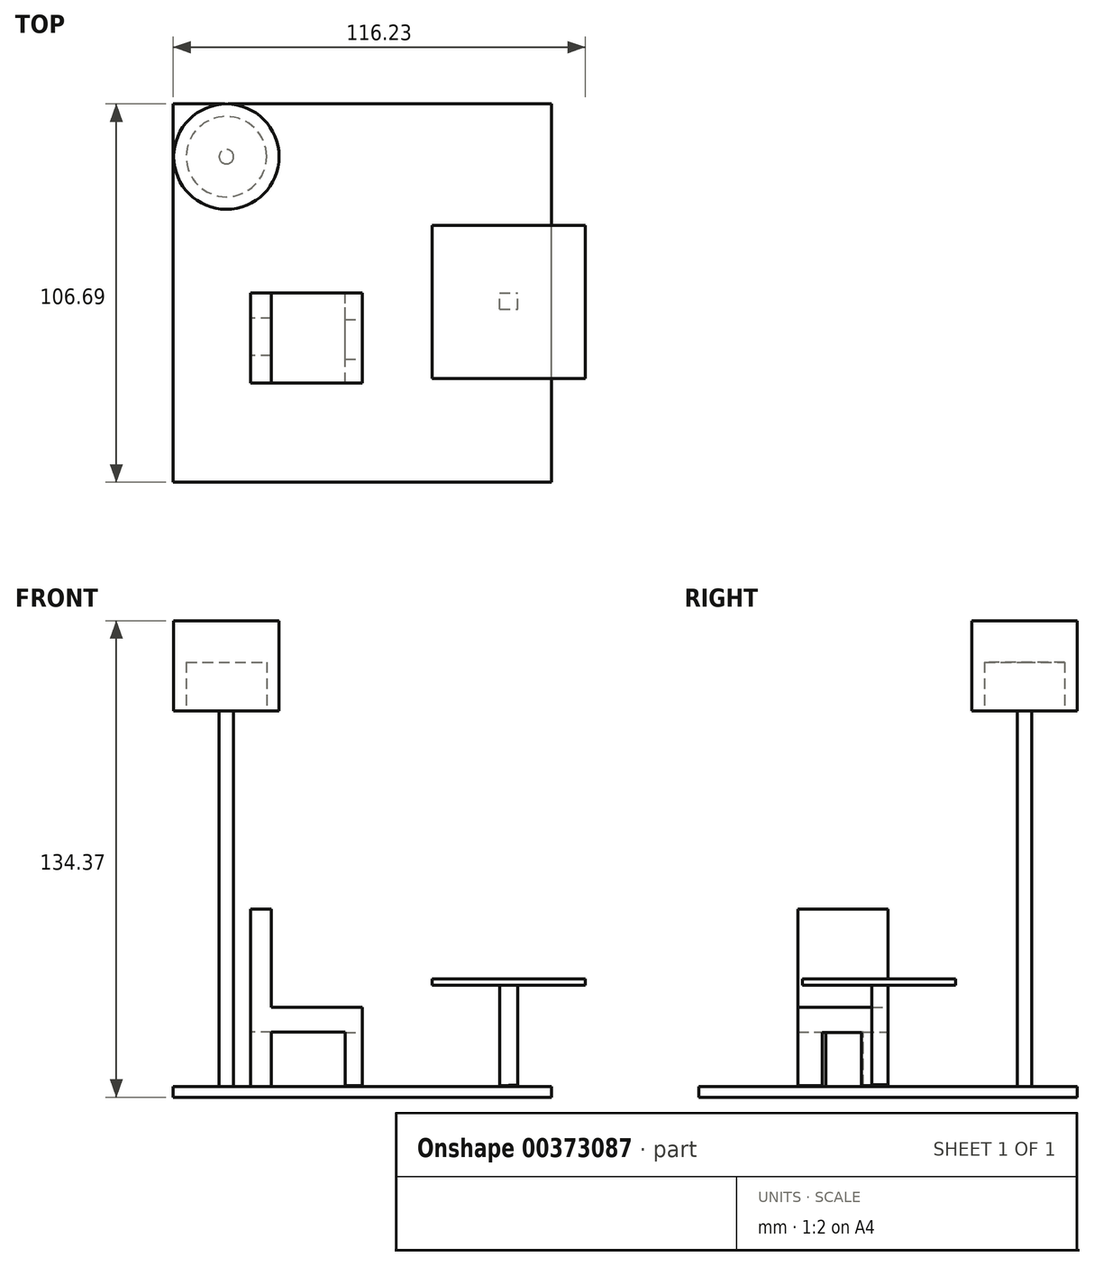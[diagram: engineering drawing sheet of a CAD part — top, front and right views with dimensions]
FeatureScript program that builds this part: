
annotation { "Feature Type Name" : "Feature", "Feature Type Description" : "" }
export const myFeature = defineFeature(function(context is Context, id is Id, definition is map)
    precondition{}
    {
        {
            var Q0;
            Q0=qCreatedBy(makeId("Top.planeOp"),FACE);
            var sketch = newSketch(context, id + "F0", { "sketchPlane" : qUnion([Q0])});
            skLineSegment(sketch, "E0.bottom", {"start": v(53.34, -53.34) * mm, "end": v(-53.34, -53.34) * mm});
            skLineSegment(sketch, "E0.top", {"start": v(53.34, 53.34) * mm, "end": v(-53.34, 53.34) * mm});
            skLineSegment(sketch, "E0.left", {"start": v(53.34, -53.34) * mm, "end": v(53.34, 53.34) * mm});
            skLineSegment(sketch, "E0.right", {"start": v(-53.34, -53.34) * mm, "end": v(-53.34, 53.34) * mm});
            skPoint(sketch, "E0.middle", {"position": v(0, 0) * mm});
            skSolve(sketch);
        }
        {
            var Q0;
            Q0 = qSketchRegion(id + "F0", true);
            extrude(context, id + "F1", {"entities" : qUnion([Q0]), "depth" : 3.05 * mm});
        }
        {
            var Q0;
            Q0=qCreatedBy(makeId("Front.planeOp"),FACE);
            var sketch = newSketch(context, id + "F2", { "sketchPlane" : qUnion([Q0])});
            skLineSegment(sketch, "E1", {"start": v(38.7, 3.2) * mm, "end": v(38.7, 31.55) * mm});
            skLineSegment(sketch, "E2", {"start": v(43.9, 3.5) * mm, "end": v(43.9, 31.55) * mm});
            skLineSegment(sketch, "E3", {"start": v(38.7, 31.55) * mm, "end": v(43.9, 31.55) * mm});
            skLineSegment(sketch, "E4", {"start": v(38.7, 3.2) * mm, "end": v(43.9, 3.5) * mm});
            skSolve(sketch);
        }
        {
            var Q0;
            Q0 = qSketchRegion(id + "F2", true);
            extrude(context, id + "F3", {"entities" : qUnion([Q0]), "depth" : 4.57 * mm});
        }
        {
            var Q0;
            Q0=makeQuery(id+"F3.opExtrude","SWEPT_FACE",FACE,{"disambiguationData":[OSD([sQuery(id+"F2.wireOp",EDGE,"E3")])]});
            var sketch = newSketch(context, id + "F4", { "sketchPlane" : qUnion([Q0])});
            skLineSegment(sketch, "E5.bottom", {"start": v(19.71, -24.09) * mm, "end": v(62.9, -24.09) * mm});
            skLineSegment(sketch, "E5.top", {"start": v(19.71, 19.1) * mm, "end": v(62.9, 19.1) * mm});
            skLineSegment(sketch, "E5.left", {"start": v(19.71, -24.09) * mm, "end": v(19.71, 19.1) * mm});
            skLineSegment(sketch, "E5.right", {"start": v(62.9, -24.09) * mm, "end": v(62.9, 19.1) * mm});
            skPoint(sketch, "E5.middle", {"position": v(41.3, -2.5) * mm});
            skPoint(sketch, "E5.middle.positionSnap0", {"position": v(41.3, 0) * mm});
            skPoint(sketch, "E5.centerSnap0", {"position": v(41.3, 0) * mm});
            skSolve(sketch);
        }
        {
            var Q0;
            Q0 = qSketchRegion(id + "F4", true);
            extrude(context, id + "F5", {"entities" : qUnion([Q0]), "operationType" : NewBodyOperationType.ADD, "depth" : 1.78 * mm});
        }
        {
            var Q0;
            Q0=makeQuery(id+"F1.opExtrude","CAP_FACE",FACE,{"disambiguationData":[OSD([sQuery(id+"F0.wireOp",EDGE,"E0.bottom"),sQuery(id+"F0.wireOp",EDGE,"E0.top"),sQuery(id+"F0.wireOp",EDGE,"E0.left"),sQuery(id+"F0.wireOp",EDGE,"E0.right")])],"isStart":false});
            var sketch = newSketch(context, id + "F6", { "sketchPlane" : qUnion([Q0])});
            skCircle(sketch, "E6", {"center": v(-38.3, 38.5) * mm, "radius": 2.03 * mm});
            skSolve(sketch);
        }
        {
            var Q0;
            Q0 = qSketchRegion(id + "F6", true);
            extrude(context, id + "F7", {"entities" : qUnion([Q0]), "operationType" : NewBodyOperationType.ADD, "depth" : 105.92 * mm});
        }
        {
            var Q0;
            Q0=qCreatedBy(makeId("Front.planeOp"),FACE);
            var sketch = newSketch(context, id + "F8", { "sketchPlane" : qUnion([Q0])});
            skLineSegment(sketch, "E7", {"start": v(0, 3.32) * mm, "end": v(0, 25.37) * mm});
            skLineSegment(sketch, "E8", {"start": v(0, 25.37) * mm, "end": v(-25.58, 25.37) * mm});
            skLineSegment(sketch, "E9", {"start": v(-25.58, 25.37) * mm, "end": v(-25.58, 53.1) * mm});
            skLineSegment(sketch, "E10", {"start": v(-25.58, 53.1) * mm, "end": v(-31.5, 53.1) * mm});
            skLineSegment(sketch, "E11", {"start": v(-31.5, 53.1) * mm, "end": v(-31.5, 3.05) * mm});
            skLineSegment(sketch, "E12", {"start": v(-31.5, 3.05) * mm, "end": v(-25.58, 3.05) * mm});
            skLineSegment(sketch, "E13", {"start": v(-25.58, 3.05) * mm, "end": v(-25.58, 18.37) * mm});
            skLineSegment(sketch, "E14", {"start": v(0, 3.32) * mm, "end": v(-4.85, 3.32) * mm});
            skLineSegment(sketch, "E15", {"start": v(-25.58, 18.37) * mm, "end": v(-4.85, 18.37) * mm});
            skLineSegment(sketch, "E16", {"start": v(-4.85, 18.37) * mm, "end": v(-4.85, 3.32) * mm});
            skSolve(sketch);
        }
        {
            var Q0;
            Q0 = qSketchRegion(id + "F8", true);
            extrude(context, id + "F9", {"entities" : qUnion([Q0]), "depth" : 25.4 * mm});
        }
        {
            var Q0;
            Q0=makeQuery(id+"F7.opExtrude","CAP_FACE",FACE,{"disambiguationData":[OSD([sQuery(id+"F6.wireOp",EDGE,"E6")])],"isStart":false});
            var sketch = newSketch(context, id + "F10", { "sketchPlane" : qUnion([Q0])});
            skCircle(sketch, "E17", {"center": v(-38.3, 38.5) * mm, "radius": 14.85 * mm});
            skSolve(sketch);
        }
        {
            var Q0;
            Q0 = qSketchRegion(id + "F10", true);
            extrude(context, id + "F11", {"entities" : qUnion([Q0]), "operationType" : NewBodyOperationType.ADD, "depth" : 25.4 * mm});
        }
        {
            var Q0;
            Q0=makeQuery(id+"F11.opExtrude","CAP_FACE",FACE,{"disambiguationData":[OSD([sQuery(id+"F10.wireOp",EDGE,"E17")])],"isStart":true});
            var sketch = newSketch(context, id + "F12", { "sketchPlane" : qUnion([Q0])});
            skCircle(sketch, "E18", {"center": v(-38.3, -38.5) * mm, "radius": 11.33 * mm});
            skSolve(sketch);
        }
        {
            var Q0;
            Q0 = qSketchRegion(id + "F12", true);
            extrude(context, id + "F13", {"entities" : qUnion([Q0]), "operationType" : NewBodyOperationType.REMOVE, "oppositeDirection" : true, "depth" : 13.72 * mm});
        }
        {
            var Q0;
            Q0=makeQuery(id+"F9.opExtrude","SWEPT_FACE",FACE,{"disambiguationData":[OSD([sQuery(id+"F8.wireOp",EDGE,"E7")])]});
            var sketch = newSketch(context, id + "F14", { "sketchPlane" : qUnion([Q0])});
            skLineSegment(sketch, "E19", {"start": v(-18.55, 3.32) * mm, "end": v(-18.55, 18.28) * mm});
            skLineSegment(sketch, "E20", {"start": v(-7.49, 3.32) * mm, "end": v(-7.49, 18.28) * mm});
            skLineSegment(sketch, "E21", {"start": v(-18.55, 18.28) * mm, "end": v(-7.49, 18.28) * mm});
            skLineSegment(sketch, "E22", {"start": v(-7.49, 3.32) * mm, "end": v(-18.55, 3.32) * mm});
            skLineSegment(sketch, "E23", {"start": v(-18.55, 3.32) * mm, "end": v(-7.49, 3.32) * mm});
            skSolve(sketch);
        }
        {
            var Q0;
            Q0=makeQuery(id+"F14.imprint","IMPRINT",FACE,{"disambiguationData":[TD([[makeQuery(id+"F14.imprint","IMPRINT",EDGE,{"derivedFrom":sQuery(id+"F14.wireOp",EDGE,"E19")}),-1.0]])]});
            extrude(context, id + "F15", {"entities" : qUnion([Q0]), "operationType" : NewBodyOperationType.REMOVE, "oppositeDirection" : true, "depth" : 25.4 * mm});
        }
        {
            var Q0;
            Q0=makeQuery(id+"F9.opExtrude","SWEPT_FACE",FACE,{"disambiguationData":[OSD([sQuery(id+"F8.wireOp",EDGE,"E11")])]});
            var sketch = newSketch(context, id + "F16", { "sketchPlane" : qUnion([Q0])});
            skLineSegment(sketch, "E24", {"start": v(7, 3.05) * mm, "end": v(7, 18.38) * mm});
            skLineSegment(sketch, "E25", {"start": v(17.53, 3.05) * mm, "end": v(17.53, 18.38) * mm});
            skLineSegment(sketch, "E26", {"start": v(7, 18.38) * mm, "end": v(17.53, 18.38) * mm});
            skLineSegment(sketch, "E27", {"start": v(7, 3.05) * mm, "end": v(17.53, 3.05) * mm});
            skSolve(sketch);
        }
        {
            var Q0;
            Q0 = qSketchRegion(id + "F16", true);
            extrude(context, id + "F17", {"entities" : qUnion([Q0]), "operationType" : NewBodyOperationType.REMOVE, "oppositeDirection" : true, "depth" : 25.4 * mm});
        }
    });
